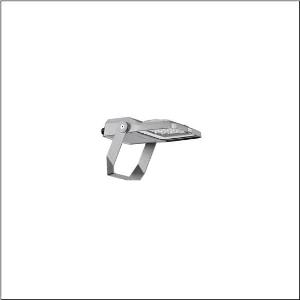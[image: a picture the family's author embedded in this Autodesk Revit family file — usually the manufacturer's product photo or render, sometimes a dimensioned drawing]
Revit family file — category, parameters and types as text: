
# Revit family: floodlight_fl_21_iq_micro___rsd12_5xa7762a4b1a_7d54
name_source: partatom
category: Lighting Fixtures
units: mm (PartAtom-declared; Revit-internal decimal feet)

## family parameters
Cut with Voids When Loaded = No
Host = Face
Light Source = No
Part Type = Normal
Room Calculation Point = No
Round Connector Dimension = Use Diameter
Shared = No

## types (1)
- --- (1 x LED, 3220 lm, 23.1 W, 4000K)
    Apparent Load = 23 VA
    CIE Flux Codes = 79 92 99 100 100
    Color Rendering = 70
    Color Temperature = 4000K
    Default Elevation = 1800 mm
    Description = Floodlight FL 21 iQ micro, floodlight, primary light control with lens, of PMMA, primary optical cover: protective disc, of toughened safety glass, transparent, light distribution: RSD12, light emission: direct distribution, installation type: surface-mounted, LED, High Power LED, rated luminous flux: 3.220lm, luminous efficacy: 139lm/W, light colour: 740, colour temperature: 4000K, control: Auto-Match, Temp-Guard, Night-Set, Smart-Wire, Desk-Remote (wireless, voltage-free reading and setting of iQ features in the workshop via application-optimized NFC function/RFID function), optimised constant luminous flux control (CLO 2.0), Street-Remote, with terminal, 6-pole, mains connection: 220..240V, AC, 50/60Hz, start of lifetime: 23W, end of service life: 24W, reduction: 11W, luminaire housing, of diecast aluminium, powder-coated, Siteco® metallic grey (DB 702S), corrosivity category C5 mid according to DIN EN ISO 12944, sealing non-destructively replaceable, mounting bracket, of steel, galvanised, powder-coated, Siteco® metallic grey (DB 702S), protection rating (complete): IP66, insulation class (complete): insulation class II (safety insulation), certification: CE, ENEC, VDE, protection symbol: D, impact resistance: IK07, permissible operating ambient temperature: -40..+40°C, permissible operating ambient temperature for outdoor applications: -40..+50°C, standard: DIN EN 12944, LABS conformity tested according to VDMA 24364:2018-05, packaging unit: 1 piece

Light Distribution: RSD12
    Height = 65 mm
    Lamp = 1 x LED
    Lamp Light Flux = 3220 lm
    Lamp Power = 23.1 W
    Lamp count = 1
    Length = 312 mm
    Luminous efficacy = 139 lm/W
    Manufacturer = Siteco
    ModVariant = No
    Model = 5XA7762A4B1A
    Mounting Place = Wall
    Mounting Type = Surface mounted
    Number of Poles = 1
    OnlyDefault = Yes
    Power Factor = 1
    Product Name = Floodlight FL 21 iQ micro | RSD12
    Product group = floodlight | wall mounted
    ProductGroupID = 2001
    Protection Class = Protection class II
    Protection Degree = IP 66
    RLX_Detail_Level = 1
    RLX_Emergency_Light_Flux = 0 lm
    RLX_Emergency_Type = 0
    RLX_Emergency_Type_DB = No
    RlxData = <blob elided: 74921 chars, md5=e0d0306d>
    Socket = socket
    Standby Power = 0 W
    System Light Flux = 3220 lm
    System Power = 23 W
    Type Comments = factory setting: luminous flux: 100 % | dim-lin: 254 | 455 mA
    Type Image = l_1006880.jpg
    URL = http://relux.com
    VarID = @adj_114901
    Voltage = 0 V
    Weight = 0.00 kg
    Width = 230 mm

## geometry (parser evidence)
native form markers: Blend x4, Sweep x12
no freeform markers — native parametric forms only
